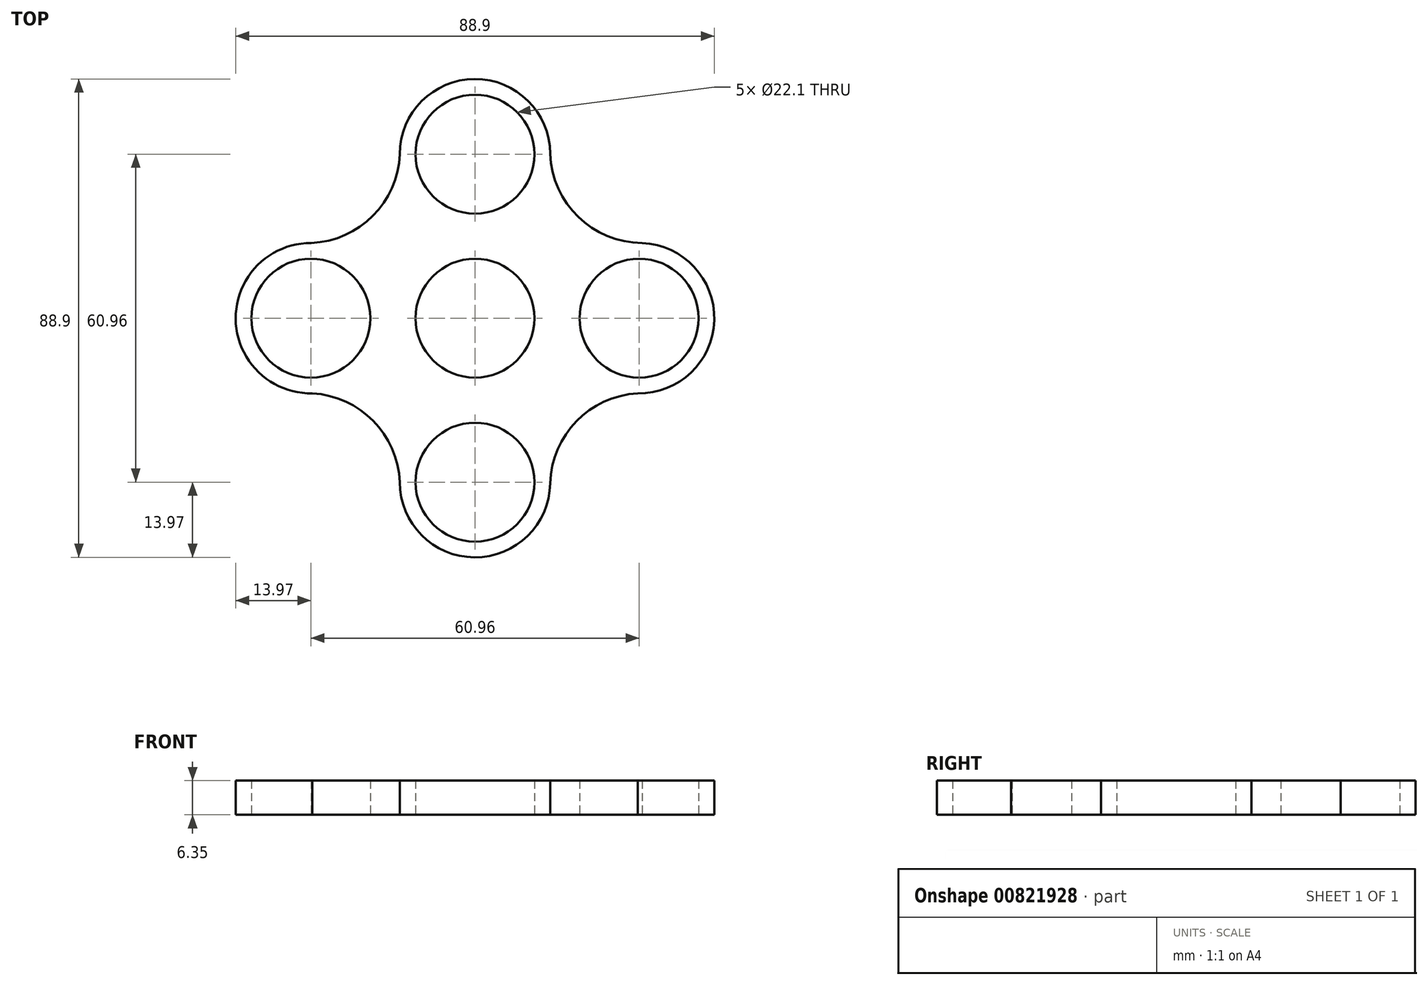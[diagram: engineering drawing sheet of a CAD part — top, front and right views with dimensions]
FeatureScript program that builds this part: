
annotation { "Feature Type Name" : "Feature", "Feature Type Description" : "" }
export const myFeature = defineFeature(function(context is Context, id is Id, definition is map)
    precondition{}
    {
        {
            var Q0;
            Q0=qCreatedBy(makeId("Top.planeOp"),FACE);
            var sketch = newSketch(context, id + "F0", { "sketchPlane" : qUnion([Q0])});
            skCircle(sketch, "E0", {"center": v(0, 0) * mm, "radius": 44.45 * mm});
            skCircle(sketch, "E1", {"center": v(0, 0) * mm, "radius": 11.05 * mm});
            skLineSegment(sketch, "E2", {"start": v(0, 0) * mm, "end": v(0, 30.48) * mm});
            skLineSegment(sketch, "E3", {"start": v(0, 0) * mm, "end": v(30.48, 0) * mm});
            skLineSegment(sketch, "E4", {"start": v(0, 0) * mm, "end": v(0, -30.48) * mm});
            skLineSegment(sketch, "E5", {"start": v(0, 0) * mm, "end": v(-30.48, 0) * mm});
            skCircle(sketch, "E6", {"center": v(0, 30.48) * mm, "radius": 11.05 * mm});
            skCircle(sketch, "E7", {"center": v(0, -30.48) * mm, "radius": 11.05 * mm});
            skCircle(sketch, "E8", {"center": v(30.48, 0) * mm, "radius": 11.05 * mm});
            skCircle(sketch, "E9", {"center": v(-30.48, 0) * mm, "radius": 11.05 * mm});
            skCircle(sketch, "E10", {"center": v(0, 30.48) * mm, "radius": 13.97 * mm});
            skCircle(sketch, "E11", {"center": v(-30.48, 0) * mm, "radius": 13.97 * mm});
            skCircle(sketch, "E12", {"center": v(0, -30.48) * mm, "radius": 13.97 * mm});
            skCircle(sketch, "E13", {"center": v(30.48, 0) * mm, "radius": 13.97 * mm});
            skCircle(sketch, "E14", {"center": v(0, 0) * mm, "radius": 16.5 * mm});
            skArc(sketch, "E15", {"start": v(13.97, 30.55) * mm, "mid": v(19.18, 18.83) * mm, "end": v(31.04, 13.96) * mm});
            skArc(sketch, "E16", {"start": v(30.23, -13.97) * mm, "mid": v(18.84, -19.15) * mm, "end": v(13.97, -30.67) * mm});
            skArc(sketch, "E17", {"start": v(-13.97, -30.48) * mm, "mid": v(-18.9, -19.09) * mm, "end": v(-30.2, -13.97) * mm});
            skArc(sketch, "E18", {"start": v(-30.42, 13.97) * mm, "mid": v(-18.98, 19.02) * mm, "end": v(-13.97, 30.48) * mm});
            skSolve(sketch);
        }
        {
            var Q0;
            {var subQ0=sQuery(id+"F0.wireOp",EDGE,"E15");var subQ1=sQuery(id+"F0.wireOp",EDGE,"E10");var subQ2=makeQuery(id+"F0.imprint","INTERSECT",VERTEX,{"derivedFrom":[subQ1,subQ0]});Q0=makeQuery(id+"F0.imprint","IMPRINT",FACE,{"disambiguationData":[TD([[makeQuery(id+"F0.imprint","IMPRINT",EDGE,{"disambiguationData":[TD([[subQ2,-1.0]])],"derivedFrom":subQ0}),-1.0]])]});}
            var Q1;
            {var subQ0=sQuery(id+"F0.wireOp",EDGE,"E18");Q1=makeQuery(id+"F0.imprint","IMPRINT",FACE,{"disambiguationData":[TD([[makeQuery(id+"F0.imprint","IMPRINT",EDGE,{"derivedFrom":subQ0}),-1.0]])]});}
            var Q2;
            Q2=makeQuery(id+"F0.imprint","IMPRINT",FACE,{"disambiguationData":[TD([[makeQuery(id+"F0.imprint","IMPRINT",EDGE,{"derivedFrom":sQuery(id+"F0.wireOp",EDGE,"E9")}),-1.0]])]});
            var Q3;
            {var subQ0=sQuery(id+"F0.wireOp",EDGE,"E17");Q3=makeQuery(id+"F0.imprint","IMPRINT",FACE,{"disambiguationData":[TD([[makeQuery(id+"F0.imprint","IMPRINT",EDGE,{"derivedFrom":subQ0}),-1.0]])]});}
            var Q4;
            {var subQ0=sQuery(id+"F0.wireOp",EDGE,"E16");Q4=makeQuery(id+"F0.imprint","IMPRINT",FACE,{"disambiguationData":[TD([[makeQuery(id+"F0.imprint","IMPRINT",EDGE,{"derivedFrom":subQ0}),-1.0]])]});}
            var Q5;
            {var subQ0=sQuery(id+"F0.wireOp",EDGE,"E3");var subQ1=sQuery(id+"F0.wireOp",EDGE,"E1");var subQ2=makeQuery(id+"F0.imprint","INTERSECT",VERTEX,{"derivedFrom":[subQ1,subQ0]});Q5=makeQuery(id+"F0.imprint","IMPRINT",FACE,{"disambiguationData":[TD([[makeQuery(id+"F0.imprint","IMPRINT",EDGE,{"disambiguationData":[TD([[subQ2,1.0]])],"derivedFrom":subQ1}),-1.0]])]});}
            var Q6;
            {var subQ0=sQuery(id+"F0.wireOp",EDGE,"E2");var subQ1=sQuery(id+"F0.wireOp",EDGE,"E1");var subQ2=makeQuery(id+"F0.imprint","INTERSECT",VERTEX,{"derivedFrom":[subQ1,subQ0]});Q6=makeQuery(id+"F0.imprint","IMPRINT",FACE,{"disambiguationData":[TD([[makeQuery(id+"F0.imprint","IMPRINT",EDGE,{"disambiguationData":[TD([[subQ2,1.0]])],"derivedFrom":subQ1}),-1.0]])]});}
            var Q7;
            {var subQ0=sQuery(id+"F0.wireOp",EDGE,"E2");var subQ1=sQuery(id+"F0.wireOp",EDGE,"E1");var subQ2=makeQuery(id+"F0.imprint","INTERSECT",VERTEX,{"derivedFrom":[subQ1,subQ0]});Q7=makeQuery(id+"F0.imprint","IMPRINT",FACE,{"disambiguationData":[TD([[makeQuery(id+"F0.imprint","IMPRINT",EDGE,{"disambiguationData":[TD([[subQ2,-1.0]])],"derivedFrom":subQ1}),-1.0]])]});}
            var Q8;
            {var subQ0=sQuery(id+"F0.wireOp",EDGE,"E5");var subQ1=sQuery(id+"F0.wireOp",EDGE,"E1");var subQ2=makeQuery(id+"F0.imprint","INTERSECT",VERTEX,{"derivedFrom":[subQ1,subQ0]});Q8=makeQuery(id+"F0.imprint","IMPRINT",FACE,{"disambiguationData":[TD([[makeQuery(id+"F0.imprint","IMPRINT",EDGE,{"disambiguationData":[TD([[subQ2,-1.0]])],"derivedFrom":subQ1}),-1.0]])]});}
            var Q9;
            Q9=makeQuery(id+"F0.imprint","IMPRINT",FACE,{"disambiguationData":[TD([[makeQuery(id+"F0.imprint","IMPRINT",EDGE,{"derivedFrom":sQuery(id+"F0.wireOp",EDGE,"E7")}),-1.0]])]});
            var Q10;
            Q10=makeQuery(id+"F0.imprint","IMPRINT",FACE,{"disambiguationData":[TD([[makeQuery(id+"F0.imprint","IMPRINT",EDGE,{"derivedFrom":sQuery(id+"F0.wireOp",EDGE,"E8")}),-1.0]])]});
            var Q11;
            Q11=makeQuery(id+"F0.imprint","IMPRINT",FACE,{"disambiguationData":[TD([[makeQuery(id+"F0.imprint","IMPRINT",EDGE,{"derivedFrom":sQuery(id+"F0.wireOp",EDGE,"E6")}),-1.0]])]});
            extrude(context, id + "F1", {"entities" : qUnion([Q0, Q1, Q2, Q3, Q4, Q5, Q6, Q7, Q8, Q9, Q10, Q11]), "depth" : 6.35 * mm, "offsetDistance" : 25.4 * mm});
        }
    });
